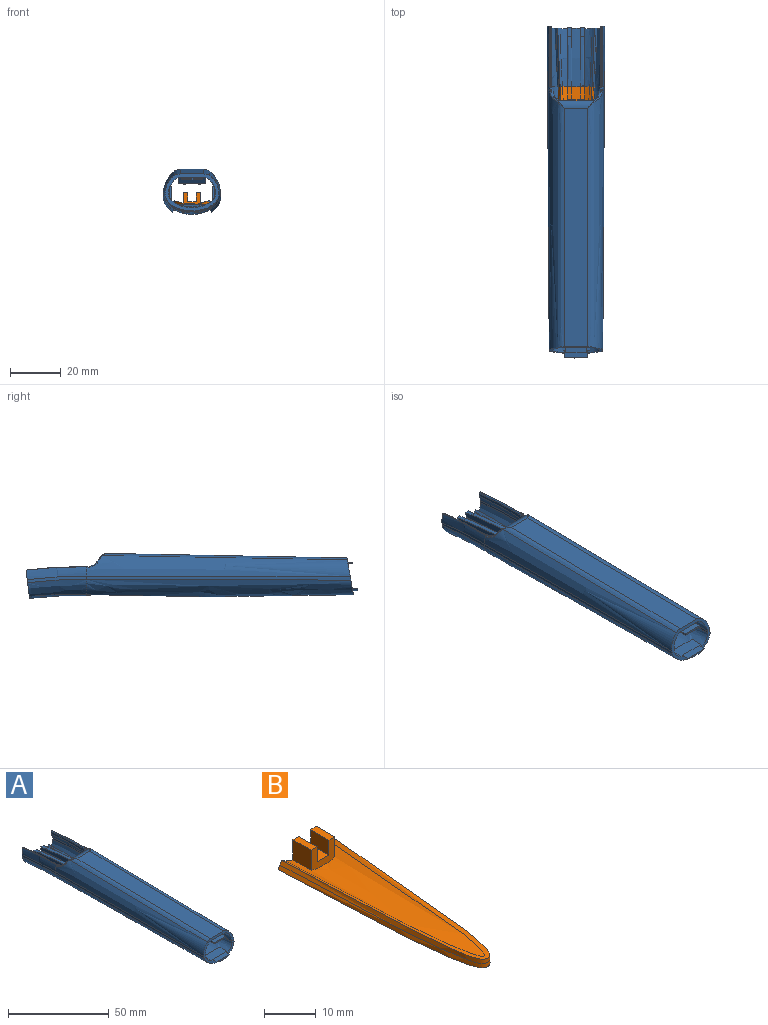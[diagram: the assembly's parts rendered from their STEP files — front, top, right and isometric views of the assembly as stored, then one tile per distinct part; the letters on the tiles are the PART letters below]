
ASSEMBLY  parts=2 mates=1
PART A: 148 faces, bbox 27x265.1x35.1 mm
  f0: bspline ~104.68x19.67mm, area 1978.4mm2, adj f11,f14,f20,f24,f88,f89,f90,f91
  f1: plane 55.11x10.94mm, normal (0,0.02,-1), area 560.8mm2, adj f12,f13,f67,f134,f135,f137,f138,f139
  f2: plane 23.73x12.12mm, normal (0,0.99,-0.13), area 80.3mm2, adj f3,f4,f5,f6,f7,f38,f40,f41
  f3: bspline ~31.46x6.04mm, area 64.1mm2, adj f2,f97,f108,f125,f126,f127
  f4: plane 23.12x4.74mm, normal (1,0,0), area 63.3mm2, adj f2,f97,f108,f128,f129
  f5: plane 23.83x6.75mm, normal (-1,0,0), area 92.4mm2, adj f2,f97,f117,f128,f129
  f6: bspline ~31.46x8.5mm, area 94.1mm2, adj f2,f97,f123,f125,f126,f127
  f7: bspline ~32.12x20.92mm, area 5.6mm2, adj f2,f37,f44,f48
  f8: plane 4.7x3.8mm, normal (0,1,0), area 9mm2, adj f9,f65,f69,f74
  f9: plane 32.69x14.57mm, normal (0,0.02,-1), area 291.9mm2, adj f8,f10,f12,f13,f26,f28,f30,f68
  f10: plane 3.8x1.78mm, normal (0,1,0), area 2.4mm2, adj f9,f65,f66,f74
  f11: bspline ~228.99x1.34mm, area 66.8mm2, adj f0,f12,f58,f134
  f12: bspline ~103.69x8.15mm, area 839.5mm2, adj f1,f9,f11,f20,f21,f29,f30,f38
  f13: bspline ~103.69x8.16mm, area 839.6mm2, adj f1,f9,f14,f23,f24,f27,f28,f42
  f14: bspline ~83.27x0.93mm, area 66.8mm2, adj f0,f13,f50,f134
  f15: plane 93.85x9.33mm, normal (0,-0.02,1), area 864.4mm2, adj f18,f19,f26,f134
  f16: bspline ~228.99x9.18mm, area 853.8mm2, adj f19,f31,f32,f44,f101,f134
  f17: bspline ~103.63x8.28mm, area 853.7mm2, adj f18,f34,f35,f40,f102,f134
  f18: bspline ~141.43x3.43mm, area 250.7mm2, adj f15,f17,f36,f134
  f19: bspline ~141.43x3.43mm, area 250.7mm2, adj f15,f16,f33,f134
  f20: bspline ~228.99x1.34mm, area 19.6mm2, adj f0,f12,f43,f60
  f21: plane 2.29x0.93mm, normal (0,1,0), area 0.6mm2, adj f12,f22,f29,f31,f47,f48
  f22: cylinder r=5.4mm len=4.85mm, axis (-1,0,0), area 2.1mm2, adj f21,f26,f29,f31
  f23: plane 2.29x0.93mm, normal (0,1,0), area 0.6mm2, adj f13,f25,f27,f34,f46,f49
  f24: bspline ~228.99x1.34mm, area 19.6mm2, adj f0,f13,f41,f53
  f25: cylinder r=5.4mm len=4.85mm, axis (-1,0,0), area 2.1mm2, adj f23,f26,f27,f34
  f26: cylinder r=4mm len=16.08mm, axis (-1,0,0), area 40.3mm2, adj f9,f15,f22,f25,f28,f30,f32,f33
  f27: bspline ~6.36x4.3mm, area 6.3mm2, adj f13,f23,f25,f28
  f28: bspline ~3.28x2.53mm, area 2.3mm2, adj f9,f13,f26,f27
  f29: bspline ~6.36x4.3mm, area 6.3mm2, adj f12,f21,f22,f30
  f30: bspline ~3.42x2.68mm, area 2.3mm2, adj f9,f12,f26,f29
  f31: bspline ~6.57x4.71mm, area 4.1mm2, adj f16,f21,f22,f32,f37
  f32: bspline ~2.91x2.89mm, area 1.2mm2, adj f16,f26,f31,f33
  f33: bspline ~2.61x2.59mm, area 0.5mm2, adj f19,f26,f32
  f34: bspline ~6.57x4.71mm, area 4.1mm2, adj f17,f23,f25,f35,f39
  f35: bspline ~2.91x2.89mm, area 1.2mm2, adj f17,f26,f34,f36
  f36: bspline ~2.52x2.5mm, area 0.5mm2, adj f18,f26,f35
  f37: plane 0.41x0.34mm, normal (0,-1,0), area 0mm2, adj f7,f31,f44,f48
  f38: bspline ~31.9x5.15mm, area 44.4mm2, adj f2,f12,f43,f47
  f39: plane 0.41x0.34mm, normal (0,-1,0), area 0mm2, adj f34,f40,f45,f49
  f40: bspline ~23.79x5.04mm, area 91.7mm2, adj f2,f17,f39,f45,f118
  f41: bspline ~23.3x2.24mm, area 22.2mm2, adj f2,f24,f42,f122
  f42: bspline ~31.9x5.15mm, area 44.4mm2, adj f2,f13,f41,f46
  f43: bspline ~31.46x3.53mm, area 22.2mm2, adj f2,f20,f38,f116
  f44: bspline ~23.79x5.04mm, area 91.7mm2, adj f2,f7,f16,f37,f115
  f45: bspline ~32.12x20.92mm, area 5.6mm2, adj f2,f39,f40,f49
  f46: plane 23.86x2.59mm, normal (-1,0,0), area 33.8mm2, adj f2,f23,f42,f49
  f47: plane 23.86x2.59mm, normal (1,0,0), area 33.8mm2, adj f2,f21,f38,f48
  f48: bspline ~28.88x2.28mm, area 18.7mm2, adj f2,f7,f21,f37,f47
  f49: bspline ~28.88x2.28mm, area 18.7mm2, adj f2,f23,f39,f45,f46
  f50: plane 7.63x1.35mm, normal (0,-0.17,-0.98), area 7.1mm2, adj f13,f14,f51,f52,f53
  f51: plane 8.46x4.78mm, normal (-1,0,0), area 11.4mm2, adj f13,f50,f52,f53,f54,f55,f56,f130
  f52: plane 3.3x0.89mm, normal (0,-0.98,0.17), area 1.8mm2, adj f13,f50,f51
  f53: plane 4.8x0.96mm, normal (0,0.98,-0.17), area 3mm2, adj f13,f24,f50,f51,f131,f132,f133
  f54: plane 2.44x0.78mm, normal (0,0.98,-0.17), area 1.1mm2, adj f13,f51,f55
  f55: plane 6.27x1.11mm, normal (0,0.17,0.98), area 5.5mm2, adj f13,f51,f54,f56
  f56: plane 3.67x0.95mm, normal (0,-0.98,0.17), area 2.2mm2, adj f13,f51,f55
  f57: plane 8.46x4.78mm, normal (1,0,0), area 12mm2, adj f12,f58,f59,f60,f61,f62,f63
  f58: plane 7.63x1.35mm, normal (0,-0.17,-0.98), area 7.1mm2, adj f11,f12,f57,f59,f60
  f59: plane 3.3x0.89mm, normal (0,-0.98,0.17), area 1.8mm2, adj f12,f57,f58
  f60: plane 4.8x0.96mm, normal (0,0.98,-0.17), area 3.3mm2, adj f12,f20,f57,f58
  f61: plane 2.44x0.78mm, normal (0,0.98,-0.17), area 1.1mm2, adj f12,f57,f62
  f62: plane 6.27x1.11mm, normal (0,0.17,0.98), area 5.5mm2, adj f12,f57,f61,f63
  f63: plane 3.67x0.95mm, normal (0,-0.98,0.17), area 2.2mm2, adj f12,f57,f62
  f64: plane 10.41x3.81mm, normal (-1,0,0), area 20.7mm2, adj f12,f65,f67,f68
  f65: plane 10.86x0.5mm, normal (0,0,-1), area 5.4mm2, adj f8,f10,f64,f66,f67,f68,f72,f77
  f66: plane 10.41x3.81mm, normal (1,0,0), area 20.7mm2, adj f10,f13,f65,f67
  f67: plane 10.87x9.9mm, normal (0,-0.34,-0.94), area 114.5mm2, adj f1,f64,f65,f66
  f68: plane 3.8x1.78mm, normal (0,1,0), area 2.4mm2, adj f9,f64,f65,f69
  f69: cylinder r=2.15mm len=12mm, axis (0,-1,0), area 135.6mm2, adj f8,f9,f68,f71,f72
  f70: cylinder r=1.75mm len=12mm, axis (0,-1,0), area 131.9mm2, adj f71,f73
  f71: plane 4.3x4.13mm, normal (0,1,0), area 4.7mm2, adj f9,f69,f70
  f72: plane 1.3x0.1mm, normal (0,-1,0), area 0.1mm2, adj f65,f69
  f73: plane 3.5x3.5mm, normal (0,1,0), area 9.6mm2, adj f70
  f74: cylinder r=2.15mm len=12mm, axis (0,-1,0), area 135.6mm2, adj f8,f9,f10,f76,f77
  f75: cylinder r=1.75mm len=12mm, axis (0,-1,0), area 131.9mm2, adj f76,f78
  f76: plane 4.3x4.13mm, normal (0,1,0), area 4.7mm2, adj f9,f74,f75
  f77: plane 1.3x0.1mm, normal (0,-1,0), area 0.1mm2, adj f65,f74
  f78: plane 3.5x3.5mm, normal (0,1,0), area 9.6mm2, adj f75
  f79: plane 6x1.06mm, normal (0,-0.17,-0.98), area 3.7mm2, adj f80,f88,f89,f90
  f80: plane 6.17x2.01mm, normal (-0.77,0.11,0.63), area 7.7mm2, adj f79,f81,f88,f90
  f81: plane 6x1.06mm, normal (0,0.17,0.98), area 3.6mm2, adj f80,f88,f90,f91
  f82: plane 6x1.06mm, normal (0,0.17,0.98), area 3.6mm2, adj f83,f92,f93,f94
  f83: plane 6.17x2.01mm, normal (0.77,0.11,0.63), area 7.7mm2, adj f82,f84,f92,f94
  f84: plane 6x1.06mm, normal (0,-0.17,-0.98), area 3.7mm2, adj f83,f92,f94,f95
  f85: plane 1.05x0.03mm, normal (-1,0,0), area 0mm2, adj f86,f97,f98
  f86: offset ~230.99x17.57mm, area 401.1mm2, adj f85,f87,f96,f97,f98,f99
  f87: bspline ~11.16x6.19mm, area 0mm2, adj f86,f97,f99
  f88: plane 5.55x1.44mm, normal (0,0.98,-0.17), area 4.3mm2, adj f0,f79,f80,f81,f89,f91
  f89: plane 6.82x4.72mm, normal (-1,0,0), area 25.7mm2, adj f0,f79,f88,f90
  f90: plane 6.53x1.44mm, normal (0,-0.98,0.17), area 5.1mm2, adj f0,f79,f80,f81,f89,f91
  f91: plane 7.15x6.57mm, normal (1,0,0), area 37.2mm2, adj f0,f81,f88,f90
  f92: plane 5.55x1.44mm, normal (0,0.98,-0.17), area 4.3mm2, adj f0,f82,f83,f84,f93,f95
  f93: plane 7.15x6.57mm, normal (-1,0,0), area 37.2mm2, adj f0,f82,f92,f94
  f94: plane 6.54x1.44mm, normal (0,-0.98,0.17), area 5.1mm2, adj f0,f82,f83,f84,f93,f95
  f95: plane 6.82x4.72mm, normal (1,0,0), area 25.7mm2, adj f0,f84,f92,f94
  f96: bspline ~56.35x13.51mm, area 99mm2, adj f0,f86,f100,f103
  f97: plane 6.41x6.27mm, normal (0,-1,0), area 28mm2, adj f3,f4,f5,f6,f85,f86,f87,f108
  f98: bspline ~2.99x2.01mm, area 2.7mm2, adj f85,f86,f104,f117
  f99: bspline ~3.05x2.05mm, area 2.8mm2, adj f86,f87,f105,f123
  f100: bspline ~1.39x1.39mm, area 1mm2, adj f0,f96,f104,f111
  f101: bspline ~103.89x1.44mm, area 137.9mm2, adj f16,f106,f115,f134
  f102: bspline ~228.99x1.71mm, area 137.9mm2, adj f17,f106,f118,f134
  f103: bspline ~1.39x1.39mm, area 1mm2, adj f0,f96,f105,f121
  f104: bspline ~1.38x1.38mm, area 1mm2, adj f98,f100,f109,f110
  f105: bspline ~1.38x1.38mm, area 1mm2, adj f99,f103,f119,f120
  f106: bspline ~103.89x22.25mm, area 2402.4mm2, adj f101,f102,f112,f114,f124,f134
  f107: bspline ~228.99x15.57mm, area 444.2mm2, adj f112,f113
  f108: bspline ~30.89x3.2mm, area 73.3mm2, adj f2,f3,f4,f97
  f109: offset ~28x4.01mm, area 23mm2, adj f2,f104,f110,f117
  f110: bspline ~25.76x1.8mm, area 23mm2, adj f2,f104,f109,f111
  f111: offset ~24.85x3.67mm, area 21.6mm2, adj f0,f2,f100,f110,f116
  f112: extruded ~71.85x28.66mm, area 193.6mm2, adj f2,f106,f107,f113,f114,f124
  f113: bspline ~30.89x18.04mm, area 337.4mm2, adj f2,f107,f112
  f114: bspline ~31.28x9.39mm, area 165.1mm2, adj f2,f106,f112,f115
  f115: bspline ~31.48x3.78mm, area 28.4mm2, adj f2,f44,f101,f114
  f116: bspline ~23.18x5.27mm, area 98.6mm2, adj f0,f2,f43,f111
  f117: offset ~35x11.55mm, area 68.4mm2, adj f2,f5,f98,f109
  f118: bspline ~23.31x2.49mm, area 28.4mm2, adj f2,f40,f102,f124
  f119: offset ~28.01x4.02mm, area 23mm2, adj f2,f105,f120,f123
  f120: bspline ~25.45x1.91mm, area 23mm2, adj f2,f105,f119,f121
  f121: offset ~24.85x3.64mm, area 21.6mm2, adj f0,f2,f103,f120,f122
  f122: bspline ~31.31x7.67mm, area 97.2mm2, adj f0,f2,f41,f121
  f123: offset ~35x11.55mm, area 69.6mm2, adj f2,f6,f99,f119
  f124: bspline ~31.28x9.39mm, area 163.7mm2, adj f2,f106,f112,f118
  f125: bspline ~11.16x1.6mm, area 0.4mm2, adj f3,f6,f97,f126
  f126: bspline ~19.35x2.07mm, area 31.1mm2, adj f3,f6,f125,f127
  f127: plane 3.61x1.62mm, normal (0,0.16,0.99), area 5.8mm2, adj f2,f3,f6,f126
  f128: plane 3.6x1.6mm, normal (0,0.16,0.99), area 5.8mm2, adj f2,f4,f5,f129
  f129: bspline ~19.53x2.07mm, area 31.4mm2, adj f4,f5,f97,f128
  f130: plane 2.12x0.14mm, normal (0,1,0), area 0.3mm2, adj f51,f131,f132,f133
  f131: plane 0.14x0.13mm, normal (-0.01,0,1), area 0mm2, adj f51,f53,f130,f133
  f132: cylinder r=19.35mm len=0.5mm, axis (0,-1,0), area 0.1mm2, adj f51,f53,f130,f133
  f133: plane 1.88x0.46mm, normal (-1,0,-0.01), area 0.5mm2, adj f53,f130,f131,f132
  f134: plane 24.43x17.83mm, normal (0,-0.98,0.17), area 70.8mm2, adj f0,f1,f11,f12,f13,f14,f15,f16
  f135: plane 8x1.17mm, normal (-1,0,0), area 7.7mm2, adj f1,f136,f138,f139,f140,f141
  f136: plane 8x8mm, normal (0,0,-1), area 64mm2, adj f135,f137,f138,f141
  f137: plane 8x1.17mm, normal (1,0,0), area 7.7mm2, adj f1,f136,f138,f139,f140,f141
  f138: plane 8x1.17mm, normal (0,1,0), area 9.4mm2, adj f1,f135,f136,f137
  f139: plane 8x0.38mm, normal (0,-1,0), area 3mm2, adj f1,f135,f137,f140
  f140: plane 8x3mm, normal (0,0,1), area 24mm2, adj f135,f137,f139,f141
  f141: plane 8x0.7mm, normal (0,-1,0), area 5.6mm2, adj f135,f136,f137,f140
  f142: plane 11.35x5.01mm, normal (0,0,1), area 56mm2, adj f0,f143,f144,f146
  f143: plane 11.34x1.16mm, normal (0,1,0), area 9mm2, adj f0,f142
  f144: plane 11.1x1.11mm, normal (0,-1,0), area 3mm2, adj f0,f142,f145
  f145: extruded ~9.28x3mm, area 28.5mm2, adj f144,f146,f147
  f146: plane 9.28x3mm, normal (0,0,1), area 27.9mm2, adj f142,f145,f147
  f147: plane 9.28x0.85mm, normal (0,-1,0), area 5.3mm2, adj f145,f146
PART B: 29 faces, bbox 19.6x234.9x11.3 mm
  f0: bspline ~0.97x0.26mm, area 0mm2, adj f1,f4,f5,f6
  f1: bspline ~2.99x2.01mm, area 2.8mm2, adj f0,f5,f6,f9
  f2: bspline ~3.05x2.05mm, area 2.9mm2, adj f3,f5,f6,f7
  f3: bspline ~0.97x0.26mm, area 0mm2, adj f2,f4,f5,f6
  f4: bspline ~6.4x1.38mm, area 6.2mm2, adj f0,f3,f5,f19
  f5: offset ~151.53x19.57mm, area 337.7mm2, adj f0,f1,f2,f3,f4,f8,f20,f26
  f6: offset ~230.99x17.57mm, area 371.1mm2, adj f0,f1,f2,f3,f13,f16,f17,f18
  f7: bspline ~1.38x1.38mm, area 1mm2, adj f2,f8,f10,f14
  f8: bspline ~49.81x12.56mm, area 100.5mm2, adj f5,f7,f9,f10
  f9: bspline ~1.38x1.38mm, area 1mm2, adj f1,f8,f10,f12
  f10: offset ~52.81x14.13mm, area 101.5mm2, adj f7,f8,f9,f11
  f11: bspline ~49.83x14.68mm, area 102.4mm2, adj f10,f12,f14,f15
  f12: bspline ~1.38x1.38mm, area 1mm2, adj f9,f11,f13,f15
  f13: bspline ~48.89x12.98mm, area 100mm2, adj f6,f12,f14,f15
  f14: bspline ~1.38x1.38mm, area 1mm2, adj f7,f11,f13,f15
  f15: offset ~51.82x15.62mm, area 100.7mm2, adj f11,f12,f13,f14
  f16: plane 6.41x0.5mm, normal (0,-1,0), area 0.4mm2, adj f6,f17,f18,f19
  f17: plane 5x0.07mm, normal (-1,0,0), area 0.2mm2, adj f6,f16,f19
  f18: plane 5x0.07mm, normal (1,0,0), area 0.2mm2, adj f6,f16,f19
  f19: extruded ~6.4x5mm, area 32.4mm2, adj f4,f16,f17,f18
  f20: plane 5x4.8mm, normal (1,0,0), area 23.9mm2, adj f5,f21,f27,f28
  f21: plane 5x1.6mm, normal (0,0,1), area 8mm2, adj f20,f22,f27,f28
  f22: plane 5x3.5mm, normal (-1,0,0), area 17.5mm2, adj f21,f23,f27,f28
  f23: plane 5x3.2mm, normal (0,0,1), area 16mm2, adj f22,f24,f27,f28
  f24: plane 5x3.5mm, normal (1,0,0), area 17.5mm2, adj f23,f25,f27,f28
  f25: plane 5x1.6mm, normal (0,0,1), area 8mm2, adj f24,f26,f27,f28
  f26: plane 5x4.8mm, normal (-1,0,0), area 23.9mm2, adj f5,f25,f27,f28
  f27: plane 6.4x5.19mm, normal (0,-1,0), area 21.1mm2, adj f5,f20,f21,f22,f23,f24,f25,f26
  f28: plane 6.4x5.26mm, normal (0,1,0), area 21.5mm2, adj f5,f20,f21,f22,f23,f24,f25,f26
PLACE A t=(-57.26,106.35,-29.72)mm
PLACE B t=(-57.26,106.35,-29.72)mm
MATE fastened B.f28 <-> A.f97  axis (0,1,0) through (-54.06,-15.16,-29.81)mm
